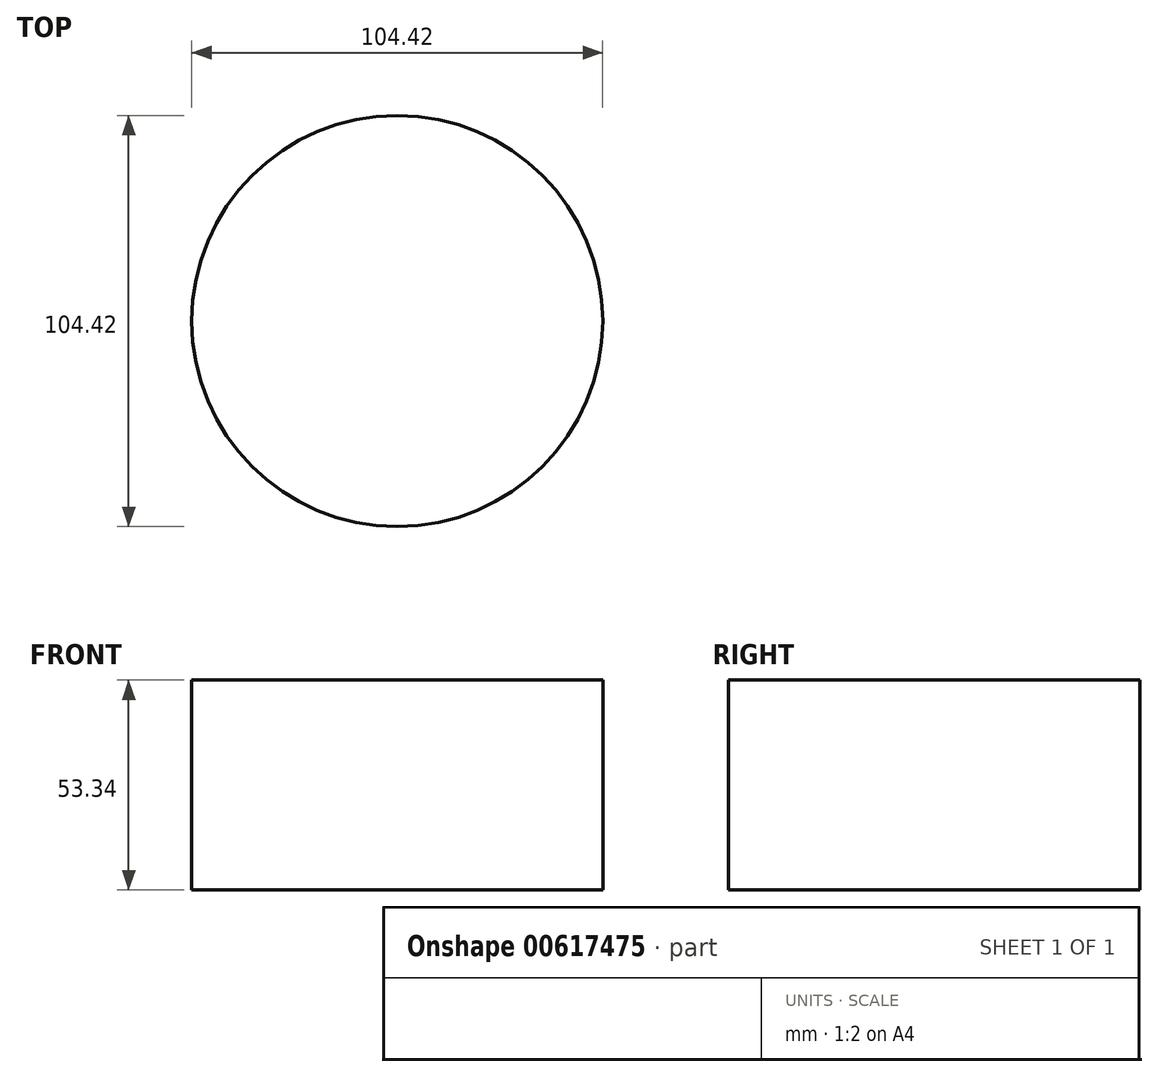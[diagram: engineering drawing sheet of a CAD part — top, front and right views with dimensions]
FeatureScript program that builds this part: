
annotation { "Feature Type Name" : "Feature", "Feature Type Description" : "" }
export const myFeature = defineFeature(function(context is Context, id is Id, definition is map)
    precondition{}
    {
        {
            var Q0;
            Q0=qCreatedBy(makeId("Top.planeOp"),FACE);
            var sketch = newSketch(context, id + "F0", { "sketchPlane" : qUnion([Q0])});
            skCircle(sketch, "E0", {"center": v(0, 0) * mm, "radius": 52.21 * mm});
            skSolve(sketch);
        }
        {
            var Q0;
            Q0 = qSketchRegion(id + "F0", true);
            extrude(context, id + "F1", {"entities" : qUnion([Q0]), "depth" : 53.34 * mm, "offsetDistance" : 25.4 * mm});
        }
    });
